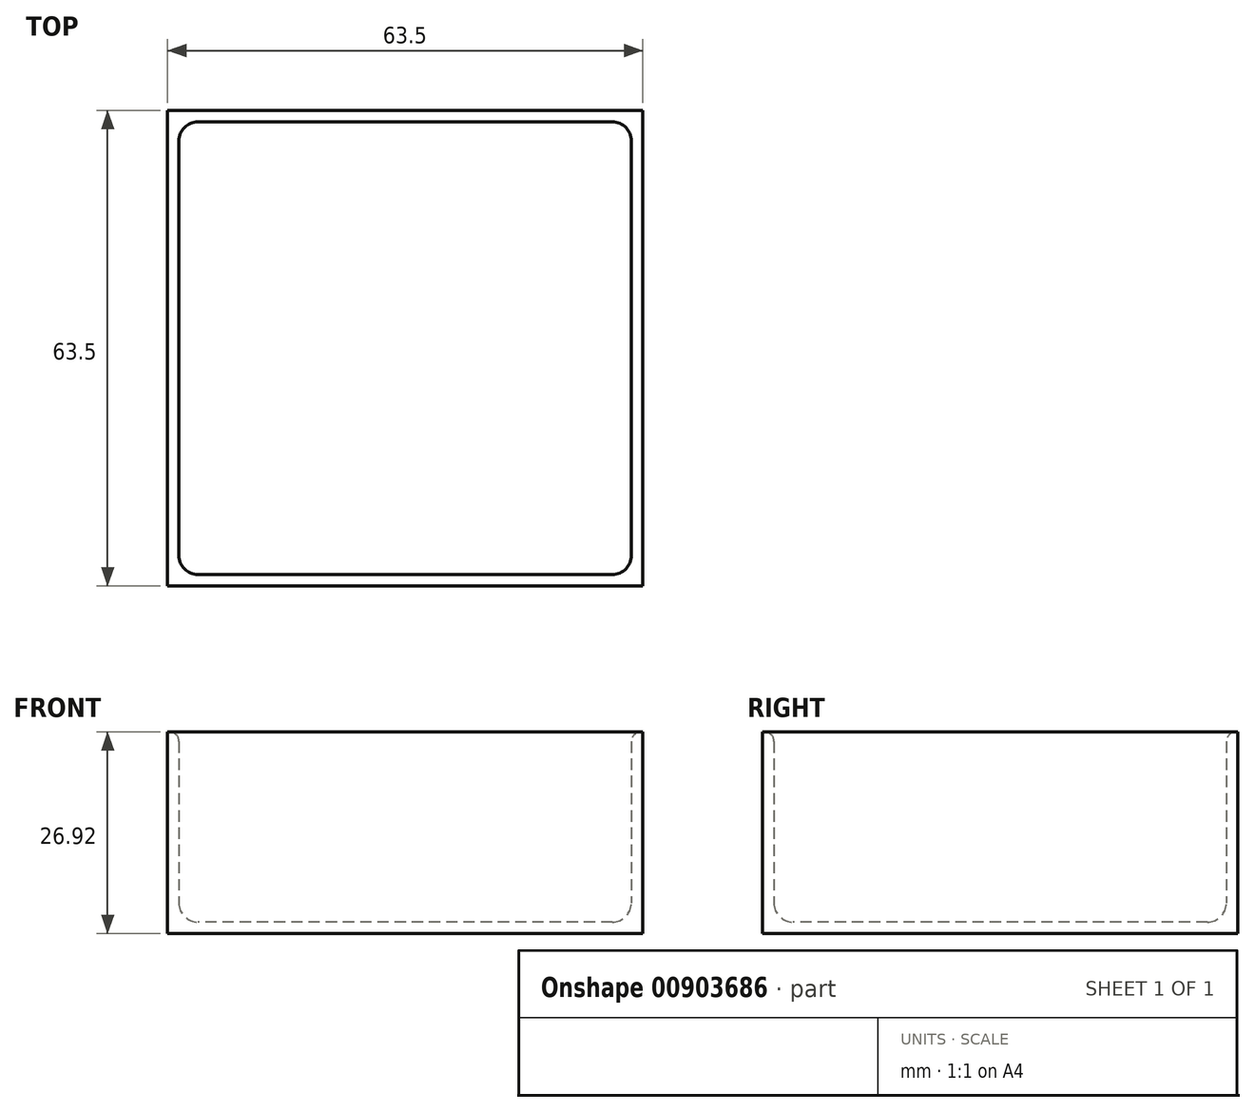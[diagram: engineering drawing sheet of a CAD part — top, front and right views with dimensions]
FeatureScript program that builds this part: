
annotation { "Feature Type Name" : "Feature", "Feature Type Description" : "" }
export const myFeature = defineFeature(function(context is Context, id is Id, definition is map)
    precondition{}
    {
        {
            var Q0;
            Q0=qCreatedBy(makeId("Top.planeOp"),FACE);
            var sketch = newSketch(context, id + "F0", { "sketchPlane" : qUnion([Q0])});
            skLineSegment(sketch, "E0.bottom", {"start": v(31.75, 31.75) * mm, "end": v(-31.75, 31.75) * mm});
            skLineSegment(sketch, "E0.top", {"start": v(31.75, -31.75) * mm, "end": v(-31.75, -31.75) * mm});
            skLineSegment(sketch, "E0.left", {"start": v(31.75, 31.75) * mm, "end": v(31.75, -31.75) * mm});
            skLineSegment(sketch, "E0.right", {"start": v(-31.75, 31.75) * mm, "end": v(-31.75, -31.75) * mm});
            skPoint(sketch, "E0.middle", {"position": v(0, 0) * mm});
            skSolve(sketch);
        }
        {
            var Q0;
            Q0=makeQuery(id+"F0.imprint","IMPRINT",FACE,{"disambiguationData":[TD([[makeQuery(id+"F0.imprint","IMPRINT",EDGE,{"derivedFrom":sQuery(id+"F0.wireOp",EDGE,"E0.bottom")}),1.0]])]});
            extrude(context, id + "F1", {"entities" : qUnion([Q0]), "depth" : 1.52 * mm, "offsetDistance" : 25.4 * mm});
        }
        {
            var Q0;
            Q0=makeQuery(id+"F1.opExtrude","CAP_FACE",FACE,{"disambiguationData":[OSD([sQuery(id+"F0.wireOp",EDGE,"E0.bottom"),sQuery(id+"F0.wireOp",EDGE,"E0.top"),sQuery(id+"F0.wireOp",EDGE,"E0.left"),sQuery(id+"F0.wireOp",EDGE,"E0.right")])],"isStart":false});
            var sketch = newSketch(context, id + "F2", { "sketchPlane" : qUnion([Q0])});
            skLineSegment(sketch, "E1.0", {"start": v(30.23, 30.23) * mm, "end": v(-30.23, 30.23) * mm});
            skLineSegment(sketch, "E1.1", {"start": v(30.23, 30.23) * mm, "end": v(30.23, -30.23) * mm});
            skLineSegment(sketch, "E1.2", {"start": v(30.23, -30.23) * mm, "end": v(-30.23, -30.23) * mm});
            skLineSegment(sketch, "E1.3", {"start": v(-30.23, 30.23) * mm, "end": v(-30.23, -30.23) * mm});
            skSolve(sketch);
        }
        {
            var Q0;
            Q0=makeQuery(id+"F2.imprint","IMPRINT",FACE,{"disambiguationData":[TD([[makeQuery(id+"F2.imprint","IMPRINT",EDGE,{"derivedFrom":sQuery(id+"F2.wireOp",EDGE,"E1.0")}),-1.0]])]});
            extrude(context, id + "F3", {"entities" : qUnion([Q0]), "operationType" : NewBodyOperationType.ADD, "depth" : 25.4 * mm, "offsetDistance" : 25.4 * mm});
        }
        {
            var Q0;
            Q0=makeQuery(id+"F1.opExtrude","CAP_FACE",FACE,{"disambiguationData":[OSD([sQuery(id+"F0.wireOp",EDGE,"E0.bottom"),sQuery(id+"F0.wireOp",EDGE,"E0.top"),sQuery(id+"F0.wireOp",EDGE,"E0.left"),sQuery(id+"F0.wireOp",EDGE,"E0.right")])],"isStart":false});
            var Q1;
            Q1=makeQuery(id+"F3.opExtrude","SWEPT_EDGE",EDGE,{"disambiguationData":[OSD([sQuery(id+"F2.wireOp",EDGE,"E1.0"),sQuery(id+"F2.wireOp",EDGE,"E1.3")])]});
            var Q2;
            Q2=makeQuery(id+"F3.opExtrude","SWEPT_EDGE",EDGE,{"disambiguationData":[OSD([sQuery(id+"F2.wireOp",EDGE,"E1.0"),sQuery(id+"F2.wireOp",EDGE,"E1.1")])]});
            var Q3;
            Q3=makeQuery(id+"F3.opExtrude","SWEPT_EDGE",EDGE,{"disambiguationData":[OSD([sQuery(id+"F2.wireOp",EDGE,"E1.1"),sQuery(id+"F2.wireOp",EDGE,"E1.2")])]});
            var Q4;
            Q4=makeQuery(id+"F3.opExtrude","SWEPT_EDGE",EDGE,{"disambiguationData":[OSD([sQuery(id+"F2.wireOp",EDGE,"E1.2"),sQuery(id+"F2.wireOp",EDGE,"E1.3")])]});
            fillet(context, id + "F4", {"entities" : qUnion([Q0, Q1, Q2, Q3, Q4]), "radius" : 2.54 * mm, "tangentPropagation" : true, "allowEdgeOverflow" : false});
        }
        {
            var Q0;
            Q0=makeQuery(id+"F3.opExtrude","CAP_EDGE",EDGE,{"disambiguationData":[OSD([sQuery(id+"F2.wireOp",EDGE,"E1.3")])],"isStart":false});
            fillet(context, id + "F5", {"entities" : qUnion([Q0]), "radius" : 1.27 * mm, "tangentPropagation" : true, "allowEdgeOverflow" : false});
        }
    });
